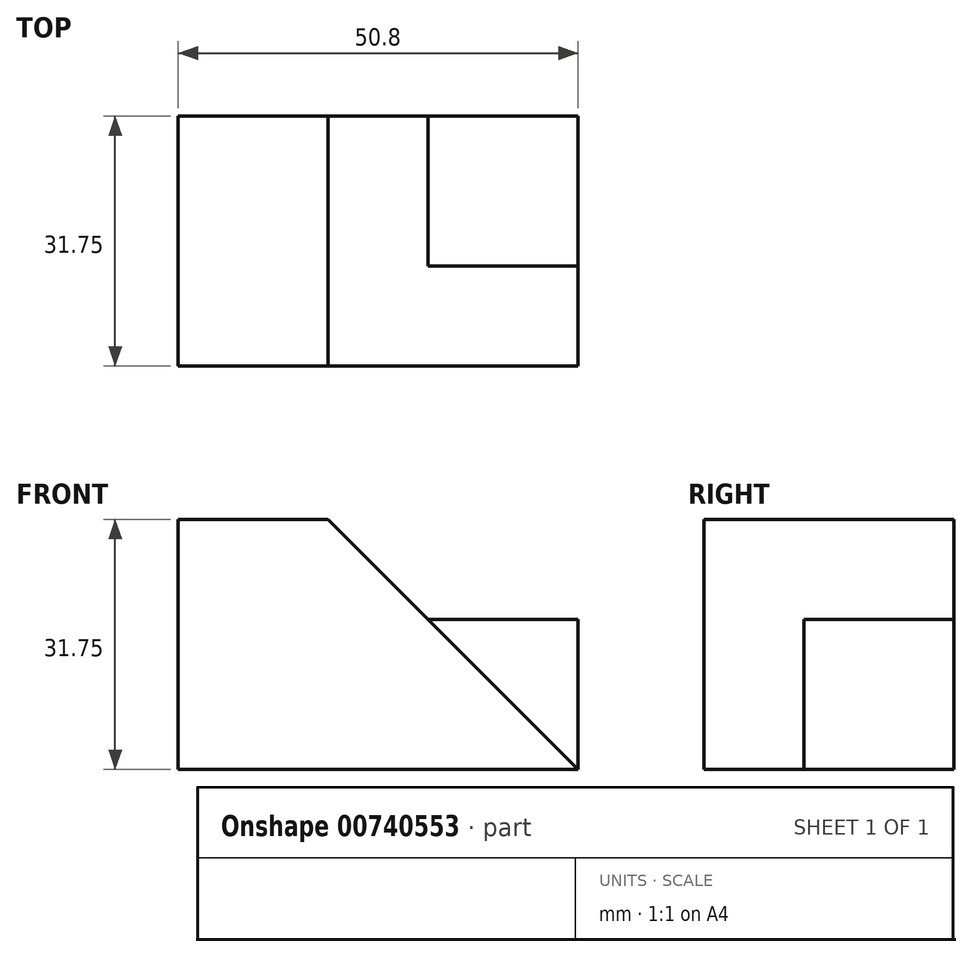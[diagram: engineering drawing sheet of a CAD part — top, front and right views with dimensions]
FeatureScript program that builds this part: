
annotation { "Feature Type Name" : "Feature", "Feature Type Description" : "" }
export const myFeature = defineFeature(function(context is Context, id is Id, definition is map)
    precondition{}
    {
        {
            var Q0;
            Q0=qCreatedBy(makeId("Front.planeOp"),FACE);
            var sketch = newSketch(context, id + "F0", { "sketchPlane" : qUnion([Q0])});
            skLineSegment(sketch, "E0.bottom", {"start": v(0, 0) * mm, "end": v(50.8, 0) * mm});
            skLineSegment(sketch, "E0.top", {"start": v(0, 31.75) * mm, "end": v(50.8, 31.75) * mm});
            skLineSegment(sketch, "E0.left", {"start": v(0, 0) * mm, "end": v(0, 31.75) * mm});
            skLineSegment(sketch, "E0.right", {"start": v(50.8, 0) * mm, "end": v(50.8, 31.75) * mm});
            skSolve(sketch);
        }
        {
            var Q0;
            Q0 = qSketchRegion(id + "F0", true);
            extrude(context, id + "F1", {"entities" : qUnion([Q0]), "depth" : 31.75 * mm, "offsetDistance" : 25.4 * mm});
        }
        {
            var Q0;
            Q0=makeQuery(id+"F1.opExtrude","CAP_FACE",FACE,{"disambiguationData":[OSD([sQuery(id+"F0.wireOp",EDGE,"E0.bottom"),sQuery(id+"F0.wireOp",EDGE,"E0.top"),sQuery(id+"F0.wireOp",EDGE,"E0.left"),sQuery(id+"F0.wireOp",EDGE,"E0.right")])],"isStart":false});
            var sketch = newSketch(context, id + "F2", { "sketchPlane" : qUnion([Q0])});
            skLineSegment(sketch, "E1", {"start": v(50.8, 0) * mm, "end": v(19.05, 31.75) * mm});
            skLineSegment(sketch, "E2", {"start": v(19.05, 31.75) * mm, "end": v(50.8, 31.75) * mm});
            skLineSegment(sketch, "E3", {"start": v(50.8, 31.75) * mm, "end": v(50.8, 0) * mm});
            skSolve(sketch);
        }
        {
            var Q0;
            Q0 = qSketchRegion(id + "F2", true);
            extrude(context, id + "F3", {"entities" : qUnion([Q0]), "operationType" : NewBodyOperationType.REMOVE, "oppositeDirection" : true, "depth" : 12.7 * mm, "offsetDistance" : 25.4 * mm});
        }
        {
            var Q0;
            Q0=makeQuery(id+"F3.boolean.opBoolean","COPY",FACE,{"derivedFrom":makeQuery(id+"F3.opExtrude","CAP_FACE",FACE,{"disambiguationData":[OSD([sQuery(id+"F2.wireOp",EDGE,"E1"),sQuery(id+"F2.wireOp",EDGE,"E2"),sQuery(id+"F2.wireOp",EDGE,"E3")])],"isStart":false})});
            var sketch = newSketch(context, id + "F4", { "sketchPlane" : qUnion([Q0])});
            skLineSegment(sketch, "E4", {"start": v(19.05, 31.75) * mm, "end": v(31.75, 19.05) * mm});
            skLineSegment(sketch, "E5", {"start": v(31.75, 19.05) * mm, "end": v(50.8, 19.05) * mm});
            skLineSegment(sketch, "E6", {"start": v(50.8, 19.05) * mm, "end": v(50.8, 31.75) * mm});
            skLineSegment(sketch, "E7", {"start": v(50.8, 31.75) * mm, "end": v(19.05, 31.75) * mm});
            skSolve(sketch);
        }
        {
            var Q0;
            Q0=makeQuery(id+"F4.imprint","IMPRINT",FACE,{"disambiguationData":[TD([[makeQuery(id+"F4.imprint","IMPRINT",EDGE,{"derivedFrom":sQuery(id+"F4.wireOp",EDGE,"E4")}),-1.0]])]});
            extrude(context, id + "F5", {"entities" : qUnion([Q0]), "operationType" : NewBodyOperationType.REMOVE, "oppositeDirection" : true, "depth" : 19.05 * mm, "offsetDistance" : 25.4 * mm});
        }
    });
